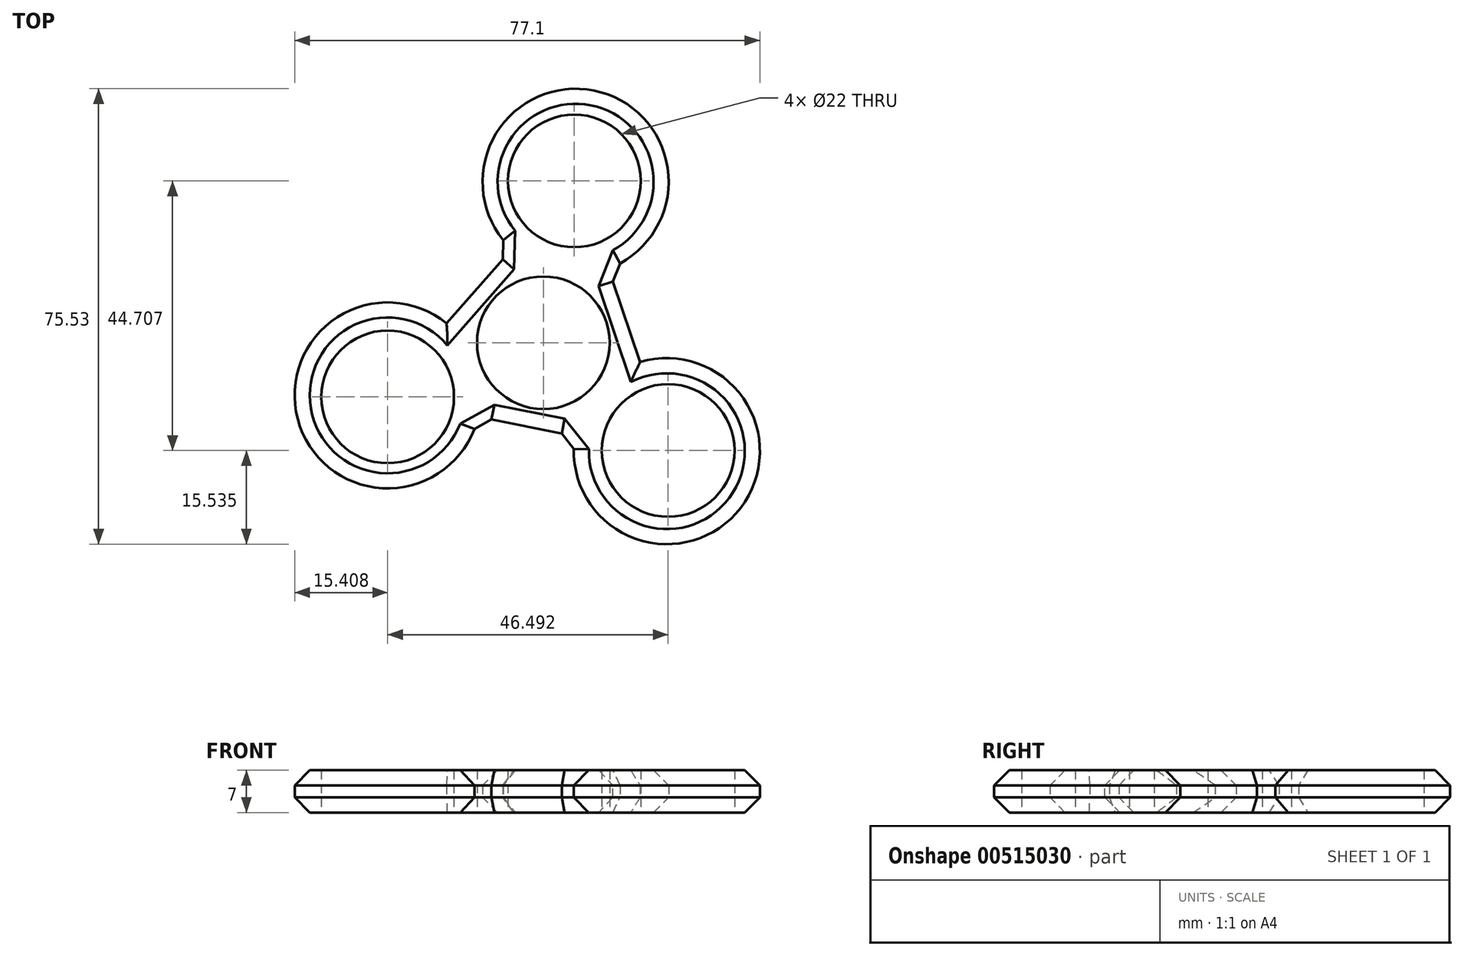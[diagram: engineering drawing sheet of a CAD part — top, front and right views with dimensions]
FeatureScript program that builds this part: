
annotation { "Feature Type Name" : "Feature", "Feature Type Description" : "" }
export const myFeature = defineFeature(function(context is Context, id is Id, definition is map)
    precondition{}
    {
        {
            var Q0;
            Q0=qCreatedBy(makeId("Top.planeOp"),FACE);
            var sketch = newSketch(context, id + "F0", { "sketchPlane" : qUnion([Q0])});
            skCircle(sketch, "E0", {"center": v(0, 0) * mm, "radius": 11 * mm});
            skCircle(sketch, "E1.cCircle", {"center": v(0, 0) * mm, "radius": 14.17 * mm, "construction": true});
            skLineSegment(sketch, "E1.0", {"start": v(10.8, 12.29) * mm, "end": v(16.04, -3.2) * mm});
            skLineSegment(sketch, "E1.1", {"start": v(16.04, -3.2) * mm, "end": v(5.24, -15.5) * mm});
            skLineSegment(sketch, "E1.2", {"start": v(5.24, -15.5) * mm, "end": v(-10.8, -12.29) * mm});
            skLineSegment(sketch, "E1.3", {"start": v(-10.8, -12.29) * mm, "end": v(-16.04, 3.2) * mm});
            skLineSegment(sketch, "E1.4", {"start": v(-16.04, 3.2) * mm, "end": v(-5.24, 15.5) * mm});
            skLineSegment(sketch, "E1.5", {"start": v(-5.24, 15.5) * mm, "end": v(10.8, 12.29) * mm});
            skPoint(sketch, "E1.0.midPoint", {"position": v(13.42, 4.54) * mm});
            skCircle(sketch, "E2", {"center": v(5.13, 26.84) * mm, "radius": 11 * mm});
            skCircle(sketch, "E3.1.0", {"center": v(-25.81, -8.98) * mm, "radius": 11 * mm});
            skCircle(sketch, "E3.2.0", {"center": v(20.68, -17.87) * mm, "radius": 11 * mm});
            skArc(sketch, "E4", {"start": v(-16.04, 3.2) * mm, "mid": v(-40.41, -13.67) * mm, "end": v(-10.8, -12.29) * mm});
            skArc(sketch, "E5.1.0", {"start": v(5.24, -15.5) * mm, "mid": v(32.04, -28.16) * mm, "end": v(16.04, -3.2) * mm});
            skArc(sketch, "E5.2.0", {"start": v(10.8, 12.29) * mm, "mid": v(8.37, 41.83) * mm, "end": v(-5.24, 15.5) * mm});
            skSolve(sketch);
        }
        {
            var Q0;
            Q0=qSketchRegion(id+"F0",true);
            extrude(context, id + "F1", {"entities" : qUnion([Q0]), "depth" : 7 * mm});
        }
        {
            var Q0;
            Q0=makeQuery(id+"F1.opExtrude","CAP_EDGE",EDGE,{"disambiguationData":[OSD([sQuery(id+"F0.wireOp",EDGE,"E1.4")])],"isStart":false});
            var Q1;
            Q1=makeQuery(id+"F1.opExtrude","CAP_EDGE",EDGE,{"disambiguationData":[OSD([sQuery(id+"F0.wireOp",EDGE,"E1.4")])],"isStart":true});
            var Q2;
            Q2=makeQuery(id+"F1.opExtrude","CAP_EDGE",EDGE,{"disambiguationData":[OSD([sQuery(id+"F0.wireOp",EDGE,"E1.0")])],"isStart":false});
            var Q3;
            Q3=makeQuery(id+"F1.opExtrude","CAP_EDGE",EDGE,{"disambiguationData":[OSD([sQuery(id+"F0.wireOp",EDGE,"E1.0")])],"isStart":true});
            var Q4;
            Q4=makeQuery(id+"F1.opExtrude","SWEPT_FACE",FACE,{"disambiguationData":[OSD([sQuery(id+"F0.wireOp",EDGE,"E1.2")])]});
            var Q5;
            Q5=makeQuery(id+"F1.opExtrude","SWEPT_FACE",FACE,{"disambiguationData":[OSD([sQuery(id+"F0.wireOp",EDGE,"E5.2.0")])]});
            chamfer(context, id + "F2", {"entities" : qUnion([Q0, Q1, Q2, Q3, Q4, Q5]), "width" : 2.5 * mm, "tangentPropagation" : true});
        }
    });
